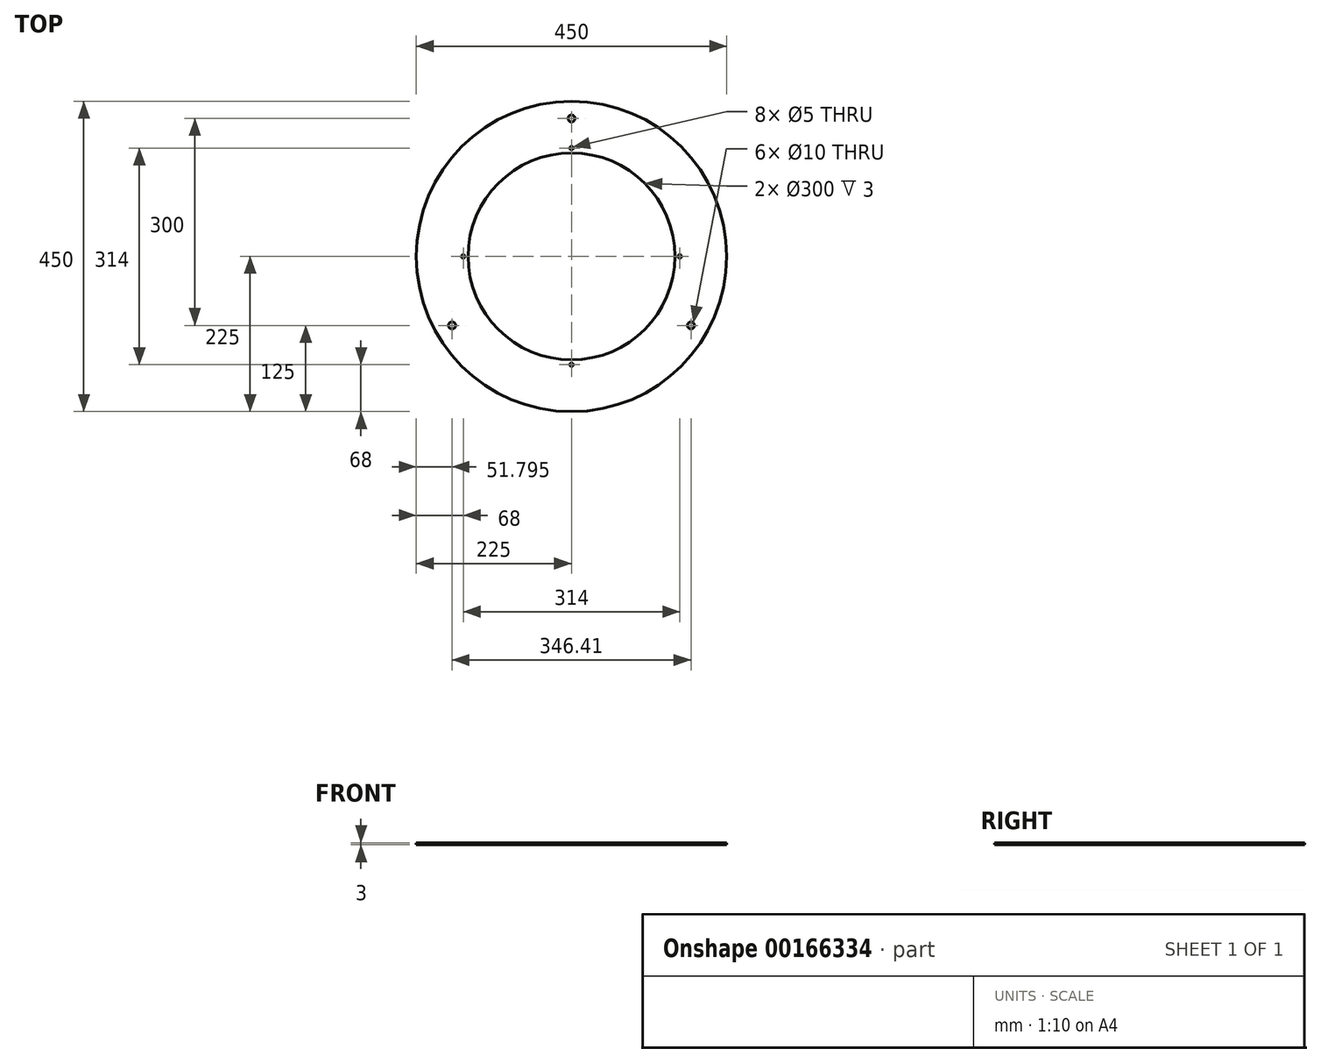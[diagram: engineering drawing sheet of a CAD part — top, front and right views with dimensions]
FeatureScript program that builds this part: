
annotation { "Feature Type Name" : "Feature", "Feature Type Description" : "" }
export const myFeature = defineFeature(function(context is Context, id is Id, definition is map)
    precondition{}
    {
        {
            var Q0;
            Q0=qCreatedBy(makeId("Top.planeOp"),FACE);
            var sketch = newSketch(context, id + "F0", { "sketchPlane" : qUnion([Q0])});
            skCircle(sketch, "E0", {"center": v(0, 0) * mm, "radius": 225 * mm});
            skCircle(sketch, "E1", {"center": v(0, 0) * mm, "radius": 150 * mm});
            skSolve(sketch);
        }
        {
            var Q0;
            Q0=makeQuery(id+"F0.imprint","IMPRINT",FACE,{"disambiguationData":[TD([[makeQuery(id+"F0.imprint","IMPRINT",EDGE,{"derivedFrom":sQuery(id+"F0.wireOp",EDGE,"E0")}),1.0]])]});
            extrude(context, id + "F1", {"entities" : qUnion([Q0]), "depth" : 3 * mm});
        }
        {
            var Q0;
            Q0=makeQuery(id+"F1.opExtrude","CAP_FACE",FACE,{"disambiguationData":[OSD([sQuery(id+"F0.wireOp",EDGE,"E0"),sQuery(id+"F0.wireOp",EDGE,"E1")])],"isStart":false});
            var sketch = newSketch(context, id + "F2", { "sketchPlane" : qUnion([Q0])});
            skLineSegment(sketch, "E2", {"start": v(0, 0) * mm, "end": v(0, 200) * mm});
            skCircle(sketch, "E3", {"center": v(0, 200) * mm, "radius": 5 * mm});
            skCircle(sketch, "E4.1.0", {"center": v(-173.2, -100) * mm, "radius": 5 * mm});
            skCircle(sketch, "E4.2.0", {"center": v(173.2, -100) * mm, "radius": 5 * mm});
            skPoint(sketch, "E4.center", {"position": v(0, 0) * mm});
            skSolve(sketch);
        }
        {
            var Q0;
            Q0 = qSketchRegion(id + "F2", true);
            extrude(context, id + "F3", {"entities" : qUnion([Q0]), "operationType" : NewBodyOperationType.REMOVE, "oppositeDirection" : true, "depth" : 3 * mm});
        }
        {
            var Q0;
            Q0=makeQuery(id+"F1.opExtrude","CAP_FACE",FACE,{"disambiguationData":[OSD([sQuery(id+"F0.wireOp",EDGE,"E0"),sQuery(id+"F0.wireOp",EDGE,"E1")])],"isStart":false});
            var sketch = newSketch(context, id + "F4", { "sketchPlane" : qUnion([Q0])});
            skLineSegment(sketch, "E5", {"start": v(0, 0) * mm, "end": v(0, 157) * mm});
            skCircle(sketch, "E6", {"center": v(0, 157) * mm, "radius": 2.5 * mm});
            skCircle(sketch, "E7.1.0", {"center": v(-157, 0) * mm, "radius": 2.5 * mm});
            skCircle(sketch, "E7.2.0", {"center": v(0, -157) * mm, "radius": 2.5 * mm});
            skCircle(sketch, "E7.3.0", {"center": v(157, 0) * mm, "radius": 2.5 * mm});
            skPoint(sketch, "E7.center", {"position": v(0, 0) * mm});
            skSolve(sketch);
        }
        {
            var Q0;
            Q0 = qSketchRegion(id + "F4", true);
            extrude(context, id + "F5", {"entities" : qUnion([Q0]), "operationType" : NewBodyOperationType.REMOVE, "oppositeDirection" : true, "depth" : 3 * mm});
        }
    });
